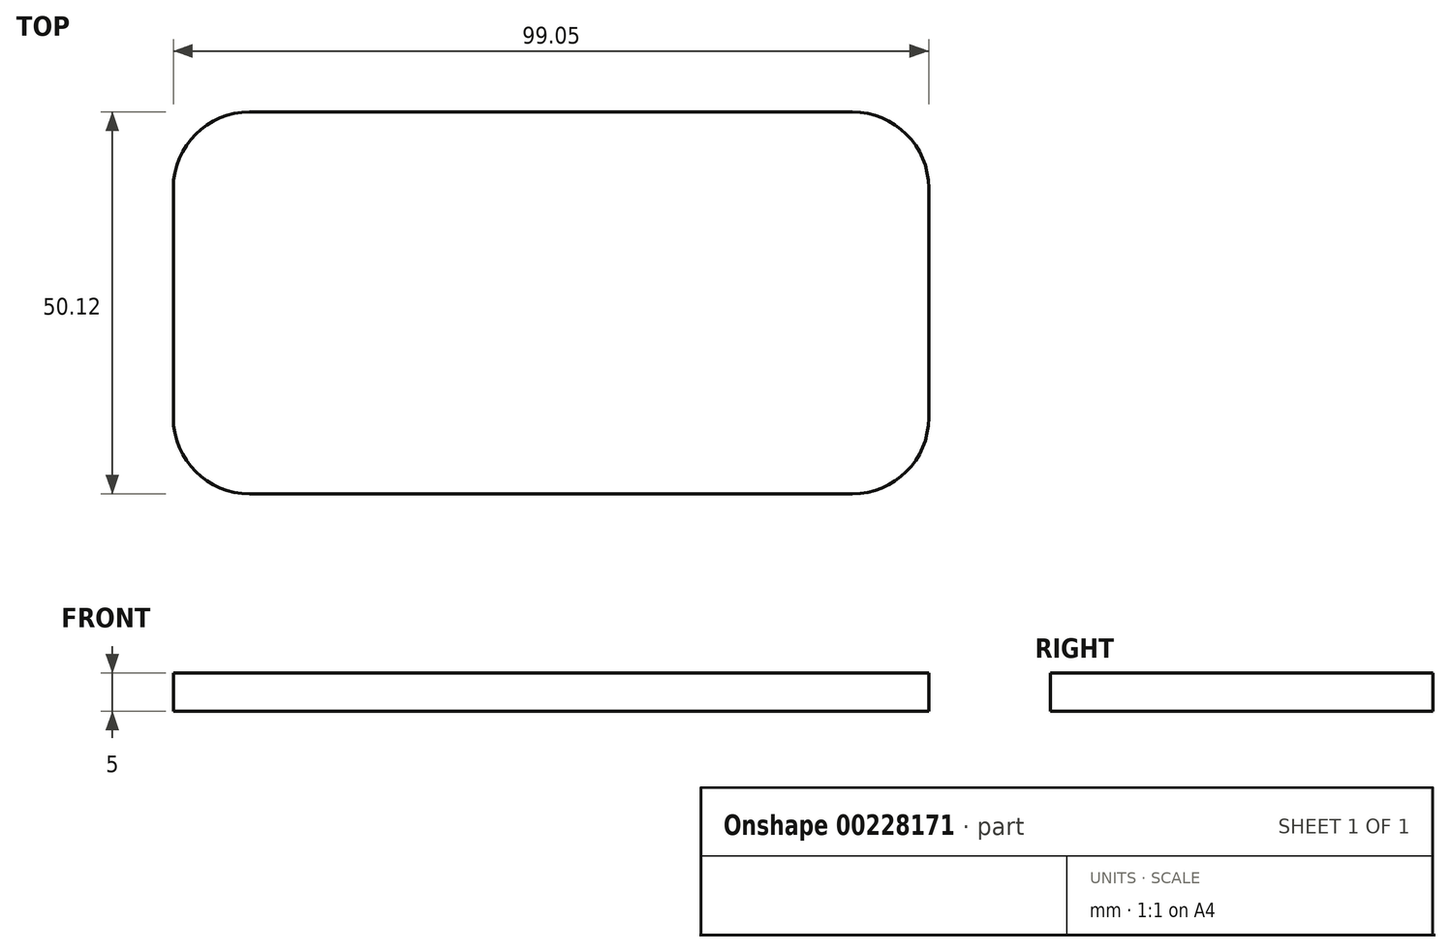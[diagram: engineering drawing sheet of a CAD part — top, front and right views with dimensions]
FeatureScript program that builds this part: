
annotation { "Feature Type Name" : "Feature", "Feature Type Description" : "" }
export const myFeature = defineFeature(function(context is Context, id is Id, definition is map)
    precondition{}
    {
        {
            var Q0;
            Q0=qCreatedBy(makeId("Top.planeOp"),FACE);
            var sketch = newSketch(context, id + "F0", { "sketchPlane" : qUnion([Q0])});
            skLineSegment(sketch, "E0.bottom", {"start": v(-33.8, 23) * mm, "end": v(45.26, 23) * mm});
            skLineSegment(sketch, "E0.top", {"start": v(-33.8, -27.13) * mm, "end": v(45.26, -27.13) * mm});
            skLineSegment(sketch, "E0.left", {"start": v(-43.8, 13) * mm, "end": v(-43.8, -17.13) * mm});
            skLineSegment(sketch, "E0.right", {"start": v(55.26, 13) * mm, "end": v(55.26, -17.13) * mm});
            skPoint(sketch, "E1.visualSharp", {"position": v(-43.8, 23) * mm});
            skArc(sketch, "E1.filletArc", {"start": v(-33.8, 23) * mm, "mid": v(-40.86, 20.06) * mm, "end": v(-43.8, 13) * mm});
            skPoint(sketch, "E2.visualSharp", {"position": v(55.26, 23) * mm});
            skArc(sketch, "E2.filletArc", {"start": v(55.26, 13) * mm, "mid": v(52.34, 20.06) * mm, "end": v(45.26, 23) * mm});
            skPoint(sketch, "E3.visualSharp", {"position": v(-43.8, -27.13) * mm});
            skArc(sketch, "E3.filletArc", {"start": v(-43.8, -17.13) * mm, "mid": v(-40.86, -24.2) * mm, "end": v(-33.8, -27.13) * mm});
            skPoint(sketch, "E4.visualSharp", {"position": v(55.26, -27.13) * mm});
            skArc(sketch, "E4.filletArc", {"start": v(45.26, -27.13) * mm, "mid": v(52.34, -24.2) * mm, "end": v(55.26, -17.13) * mm});
            skSolve(sketch);
        }
        {
            var Q0;
            Q0=makeQuery(id+"F0.imprint","IMPRINT",FACE,{"disambiguationData":[TD([[makeQuery(id+"F0.imprint","IMPRINT",EDGE,{"derivedFrom":sQuery(id+"F0.wireOp",EDGE,"E0.bottom")}),-1.0]])]});
            extrude(context, id + "F1", {"entities" : qUnion([Q0]), "depth" : 5 * mm});
        }
    });
